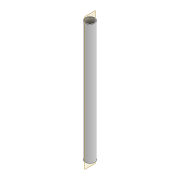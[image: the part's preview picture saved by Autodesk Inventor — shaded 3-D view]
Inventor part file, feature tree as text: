
AUTODESK INVENTOR PART (.ipt)
format: ipt  version: 2022 (Build 260153000, 153)  size: 78,336 bytes
history: native  units: mm
features: extrude x1, sketch x1
ambient origin geometry x8: Origin, YZ Plane, XZ Plane, XY Plane, X Axis, Y Axis, Z Axis, Center Point
bodies: Body1 (feature_tree)
feature tree (2):
  extrude  "Extrusion2"  Depth=150.0mm
  sketch  "Sketch2"  dims[d6=10.0mm d7=12.0mm d8=150.0mm d9=0.0mm]
